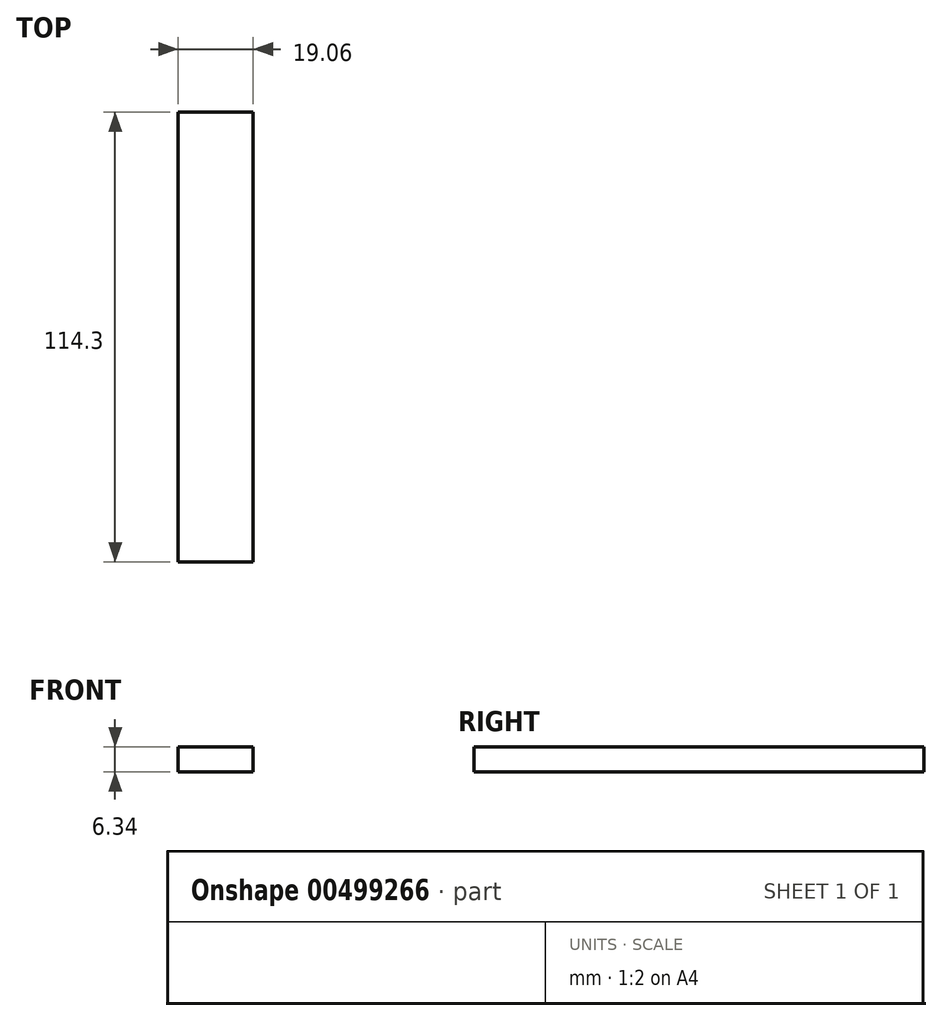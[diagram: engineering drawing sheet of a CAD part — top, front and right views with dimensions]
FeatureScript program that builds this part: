
annotation { "Feature Type Name" : "Feature", "Feature Type Description" : "" }
export const myFeature = defineFeature(function(context is Context, id is Id, definition is map)
    precondition{}
    {
        {
            var Q0;
            Q0=qCreatedBy(makeId("Front.planeOp"),FACE);
            var sketch = newSketch(context, id + "F0", { "sketchPlane" : qUnion([Q0])});
            skLineSegment(sketch, "E0.bottom", {"start": v(9.53, -3.18) * mm, "end": v(-9.52, -3.18) * mm});
            skLineSegment(sketch, "E0.top", {"start": v(9.53, 3.18) * mm, "end": v(-9.53, 3.17) * mm});
            skLineSegment(sketch, "E0.left", {"start": v(9.53, -3.18) * mm, "end": v(9.53, 3.18) * mm});
            skLineSegment(sketch, "E0.right", {"start": v(-9.53, -3.18) * mm, "end": v(-9.53, 3.17) * mm});
            skPoint(sketch, "E0.middle", {"position": v(0, 0) * mm});
            skSolve(sketch);
        }
        {
            var Q0;
            Q0 = qSketchRegion(id + "F0", true);
            extrude(context, id + "F1", {"entities" : qUnion([Q0]), "endBound" : BoundingType.SYMMETRIC, "depth" : 114.3 * mm});
        }
    });
